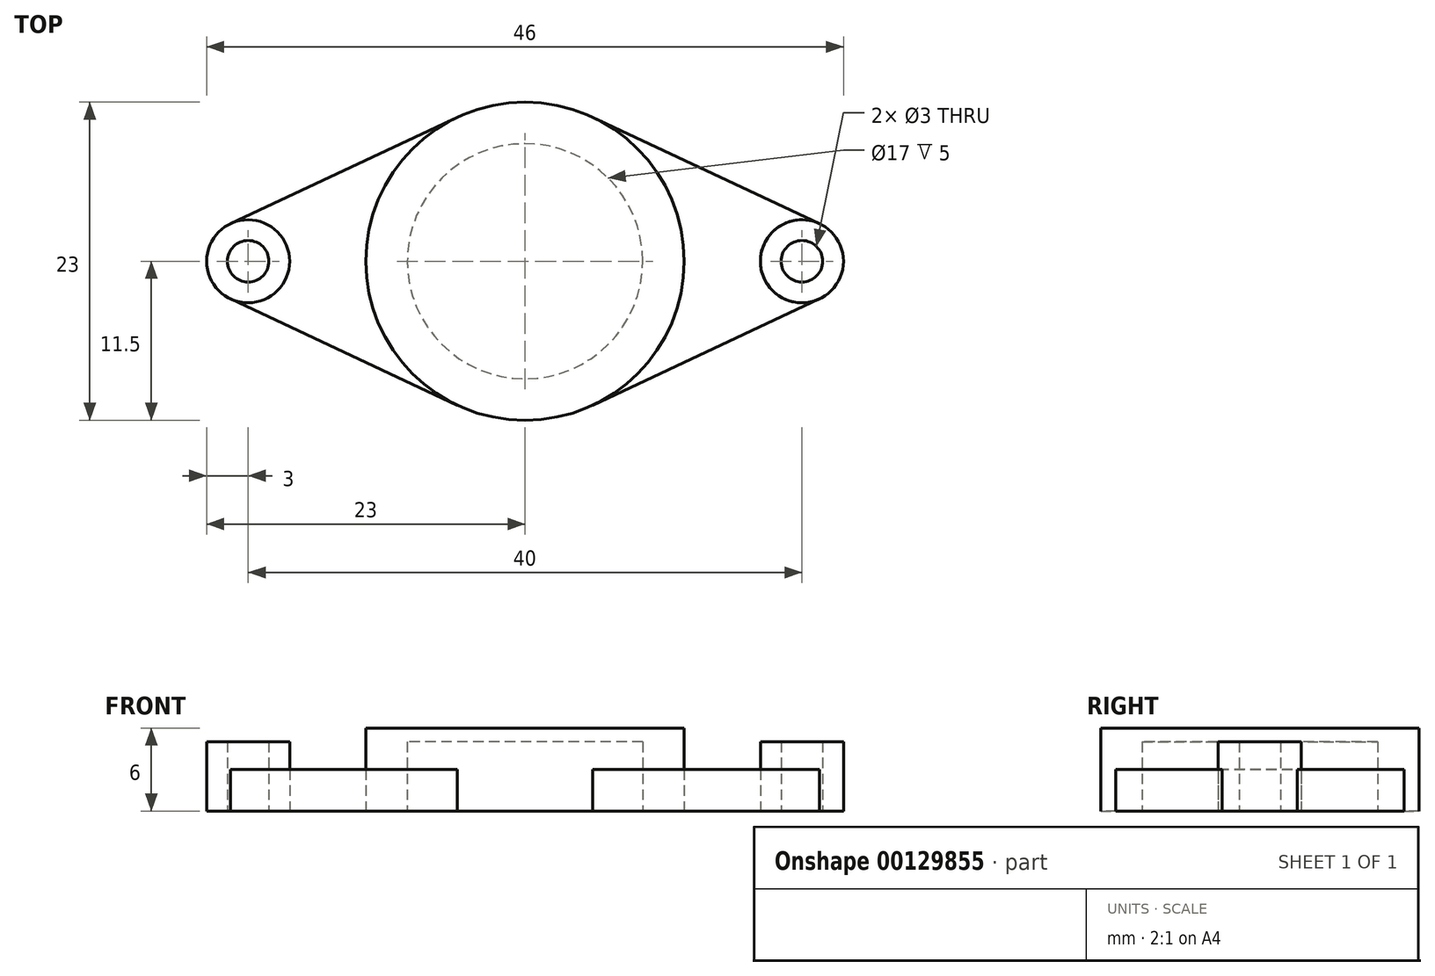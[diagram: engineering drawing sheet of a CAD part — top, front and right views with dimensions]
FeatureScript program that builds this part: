
annotation { "Feature Type Name" : "Feature", "Feature Type Description" : "" }
export const myFeature = defineFeature(function(context is Context, id is Id, definition is map)
    precondition{}
    {
        {
            var Q0;
            Q0=qCreatedBy(makeId("Top.planeOp"),FACE);
            var sketch = newSketch(context, id + "F0", { "sketchPlane" : qUnion([Q0])});
            skCircle(sketch, "E0", {"center": v(0, 0) * mm, "radius": 8.5 * mm});
            skCircle(sketch, "E1.0", {"center": v(0, 0) * mm, "radius": 11.5 * mm});
            skLineSegment(sketch, "E2", {"start": v(0, 0) * mm, "end": v(-20, 0) * mm, "construction": true});
            skLineSegment(sketch, "E3", {"start": v(0, 0) * mm, "end": v(20, 0) * mm, "construction": true});
            skCircle(sketch, "E4", {"center": v(-20, 0) * mm, "radius": 1.5 * mm});
            skCircle(sketch, "E5", {"center": v(-20, 0) * mm, "radius": 3 * mm});
            skCircle(sketch, "E6", {"center": v(20, 0) * mm, "radius": 1.5 * mm});
            skCircle(sketch, "E7", {"center": v(20, 0) * mm, "radius": 3 * mm});
            skLineSegment(sketch, "E8", {"start": v(-21.28, 2.72) * mm, "end": v(-4.89, 10.4) * mm});
            skLineSegment(sketch, "E9", {"start": v(21.28, 2.72) * mm, "end": v(4.89, 10.4) * mm});
            skLineSegment(sketch, "E10", {"start": v(-21.28, -2.72) * mm, "end": v(-4.89, -10.4) * mm});
            skLineSegment(sketch, "E11", {"start": v(21.27, -2.72) * mm, "end": v(4.89, -10.4) * mm});
            skSolve(sketch);
        }
        {
            var Q0;
            Q0=makeQuery(id+"F0.imprint","IMPRINT",FACE,{"disambiguationData":[TD([[makeQuery(id+"F0.imprint","IMPRINT",EDGE,{"derivedFrom":sQuery(id+"F0.wireOp",EDGE,"E0")}),-1.0]])]});
            var Q1;
            Q1=makeQuery(id+"F0.imprint","IMPRINT",FACE,{"disambiguationData":[TD([[makeQuery(id+"F0.imprint","IMPRINT",EDGE,{"derivedFrom":sQuery(id+"F0.wireOp",EDGE,"E0")}),1.0]])]});
            extrude(context, id + "F1", {"entities" : qUnion([Q0, Q1]), "depth" : 6 * mm});
        }
        {
            var Q0;
            Q0=makeQuery(id+"F0.imprint","IMPRINT",FACE,{"disambiguationData":[TD([[makeQuery(id+"F0.imprint","IMPRINT",EDGE,{"derivedFrom":sQuery(id+"F0.wireOp",EDGE,"E0")}),1.0]])]});
            extrude(context, id + "F2", {"entities" : qUnion([Q0]), "operationType" : NewBodyOperationType.REMOVE, "depth" : 5 * mm});
        }
        {
            var Q0;
            Q0=makeQuery(id+"F0.imprint","IMPRINT",FACE,{"disambiguationData":[TD([[makeQuery(id+"F0.imprint","IMPRINT",EDGE,{"derivedFrom":sQuery(id+"F0.wireOp",EDGE,"E4")}),-1.0]])]});
            var Q1;
            Q1=makeQuery(id+"F0.imprint","IMPRINT",FACE,{"disambiguationData":[TD([[makeQuery(id+"F0.imprint","IMPRINT",EDGE,{"derivedFrom":sQuery(id+"F0.wireOp",EDGE,"E6")}),-1.0]])]});
            extrude(context, id + "F3", {"entities" : qUnion([Q0, Q1]), "depth" : 5 * mm});
        }
        {
            var Q0;
            {var subQ0=sQuery(id+"F0.wireOp",EDGE,"E8");Q0=makeQuery(id+"F0.imprint","IMPRINT",FACE,{"disambiguationData":[TD([[makeQuery(id+"F0.imprint","IMPRINT",EDGE,{"derivedFrom":subQ0}),-1.0]])]});}
            var Q1;
            {var subQ0=sQuery(id+"F0.wireOp",EDGE,"E9");Q1=makeQuery(id+"F0.imprint","IMPRINT",FACE,{"disambiguationData":[TD([[makeQuery(id+"F0.imprint","IMPRINT",EDGE,{"derivedFrom":subQ0}),1.0]])]});}
            extrude(context, id + "F4", {"entities" : qUnion([Q0, Q1]), "depth" : 3 * mm});
        }
    });
